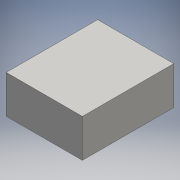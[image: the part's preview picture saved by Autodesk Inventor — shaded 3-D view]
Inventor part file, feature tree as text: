
AUTODESK INVENTOR PART (.ipt)
format: ipt  version: 2016 (Build 200138000, 138)  size: 82,432 bytes
history: native  units: mm
features: other x1, extrude x1, sketch x1
ambient origin geometry x8: Origin, YZ Plane, XZ Plane, XY Plane, X Axis, Y Axis, Z Axis, Center Point
bodies: Body1 (feature_tree)
feature tree (3):
  other  "ソリッド1"
  extrude  "押し出し1"  Depth=100.0mm
  sketch  "スケッチ1"
